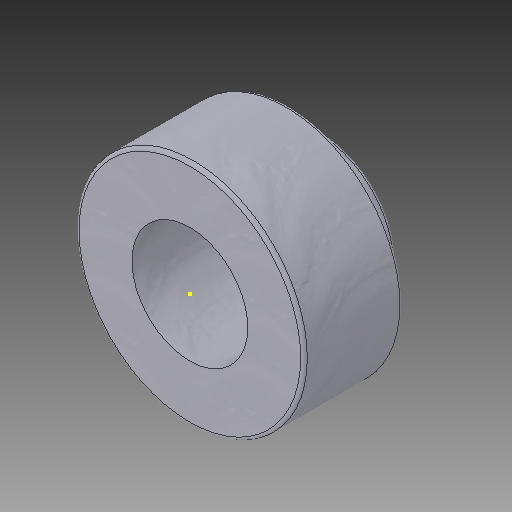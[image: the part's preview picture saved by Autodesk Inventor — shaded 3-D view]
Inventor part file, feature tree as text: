
AUTODESK INVENTOR PART (.ipt)
format: ipt  version: 2019 (Build 230136000, 136)  size: 204,800 bytes
history: native  units: in
note: dims shown in document units (in); Inventor stores cm internally (conversion verified against a paired STEP export)
features: sketch x6, other x3
ambient origin geometry x8: Origin, YZ Plane, XZ Plane, XY Plane, X Axis, Y Axis, Z Axis, Center Point
bodies: Solid1 (feature_tree)
feature tree (9):
  other  "project flange bearing part2.ipt"
  other  "Solid1::project flange bearing part2.ipt"
  other  "TaggingFeature1"
  sketch  "Sketch1"  dims[d0=0.3937in]
  sketch  "Sketch2"
  sketch  "Sketch3"
  sketch  "Sketch4"
  sketch  "Sketch5"
  sketch  "Sketch6"
